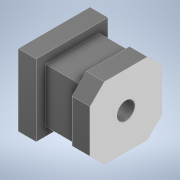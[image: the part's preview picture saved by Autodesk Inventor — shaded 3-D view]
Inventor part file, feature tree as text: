
AUTODESK INVENTOR PART (.ipt)
format: ipt  version: 2021 (Build 250183000, 183)  size: 126,464 bytes
history: native  units: mm
features: extrude x2, sketch x2, plane x1, chamfer x1
ambient origin geometry x8: Origin, YZ Plane, XZ Plane, XY Plane, X Axis, Y Axis, Z Axis, Center Point
bodies: Solid1 (feature_tree)
feature tree (6):
  extrude  "Extrusion1"  Depth=20.0mm
  plane  "Work Plane1"
  extrude  "Extrusion2"  Depth=20.0mm TaperAngle=0.0deg
  chamfer  "Chamfer1"  [1 undecoded]
  sketch  "Sketch1"  dims[d0=5.0mm d1=20.0mm]
  sketch  "Sketch2"  dims[d2=20.0mm d3=20.0mm d4=0.0mm d5=-5.0mm d6=15.0mm d7=15.0mm d8=10.0mm d9=0.0mm d10=4.0mm d11=2.0mm d12=45.0deg]
note: 1 required parameter value undecoded (feature->parameter linkage not recoverable at this tier; creation-order binding heuristic only, values carry confidence <= 0.55)
